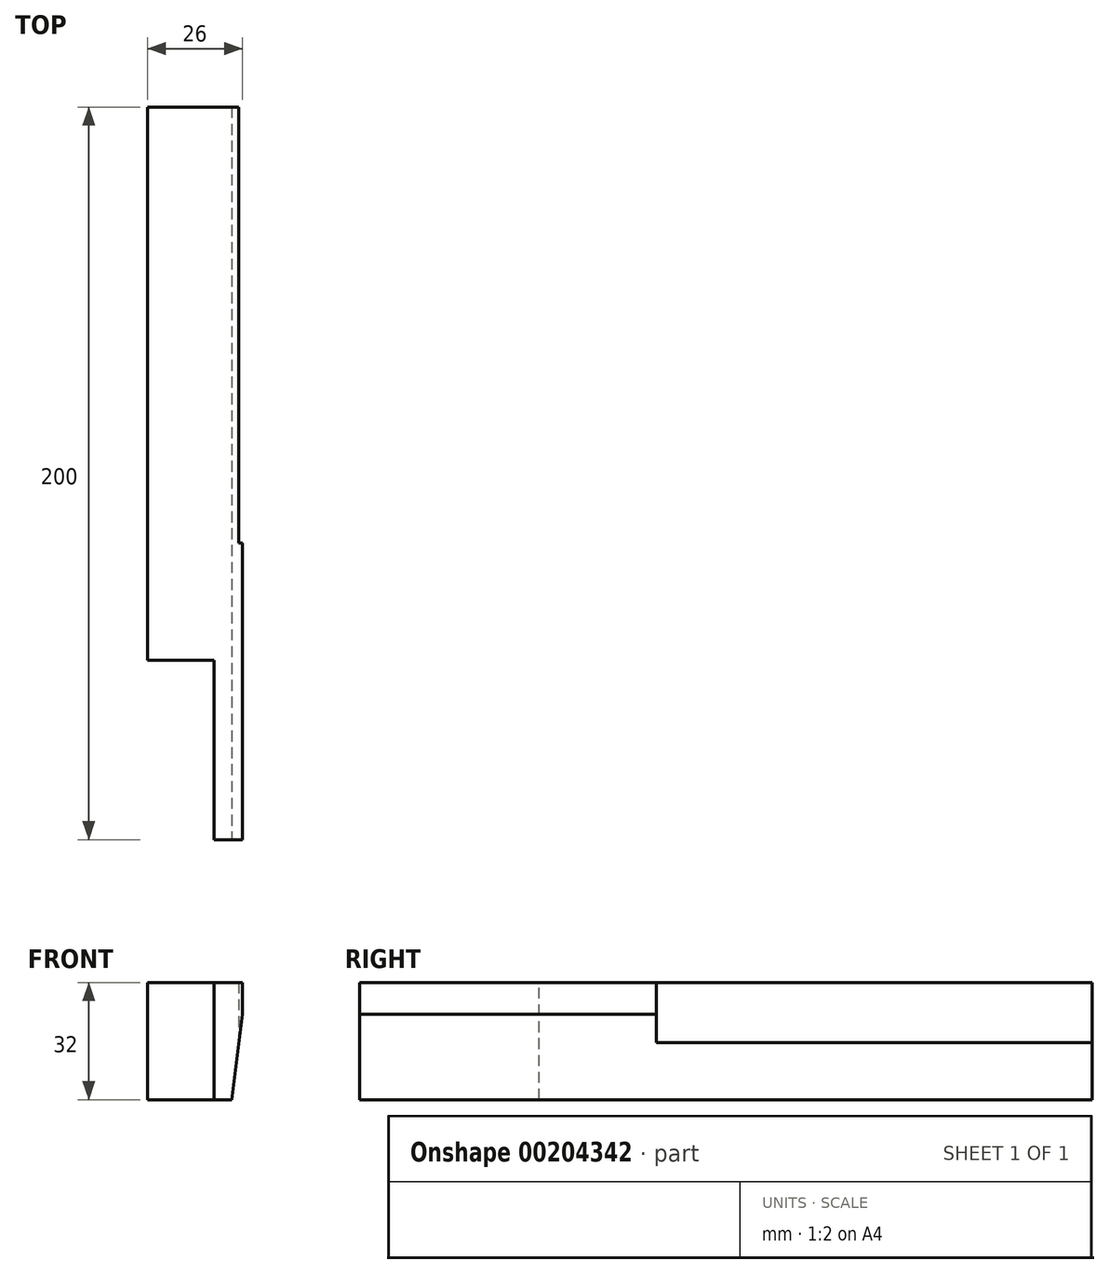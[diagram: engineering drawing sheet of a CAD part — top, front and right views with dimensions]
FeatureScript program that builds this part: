
annotation { "Feature Type Name" : "Feature", "Feature Type Description" : "" }
export const myFeature = defineFeature(function(context is Context, id is Id, definition is map)
    precondition{}
    {
        {
            var Q0;
            Q0=qCreatedBy(makeId("Front.planeOp"),FACE);
            var sketch = newSketch(context, id + "F0", { "sketchPlane" : qUnion([Q0])});
            skLineSegment(sketch, "E0.bottom", {"start": v(0, 0) * mm, "end": v(-25, 0) * mm});
            skLineSegment(sketch, "E0.top", {"start": v(0, -32) * mm, "end": v(-25, -32) * mm});
            skLineSegment(sketch, "E0.left", {"start": v(0, 0) * mm, "end": v(0, -32) * mm});
            skLineSegment(sketch, "E0.right", {"start": v(-25, 0) * mm, "end": v(-25, -32) * mm});
            skSolve(sketch);
        }
        {
            var Q0;
            Q0=makeQuery(id+"F0.imprint","IMPRINT",FACE,{"disambiguationData":[TD([[makeQuery(id+"F0.imprint","IMPRINT",EDGE,{"derivedFrom":sQuery(id+"F0.wireOp",EDGE,"E0.bottom")}),1.0]])]});
            extrude(context, id + "F1", {"entities" : qUnion([Q0]), "depth" : 151 * mm});
        }
        {
            var Q0;
            Q0=makeQuery(id+"F1.opExtrude","CAP_FACE",FACE,{"disambiguationData":[OSD([sQuery(id+"F0.wireOp",EDGE,"E0.bottom"),sQuery(id+"F0.wireOp",EDGE,"E0.top"),sQuery(id+"F0.wireOp",EDGE,"E0.left"),sQuery(id+"F0.wireOp",EDGE,"E0.right")])],"isStart":false});
            var sketch = newSketch(context, id + "F2", { "sketchPlane" : qUnion([Q0])});
            skLineSegment(sketch, "E1.bottom", {"start": v(0, -32) * mm, "end": v(-6.8, -32) * mm});
            skLineSegment(sketch, "E1.top", {"start": v(0, 0) * mm, "end": v(-6.8, 0) * mm});
            skLineSegment(sketch, "E1.left", {"start": v(0, -32) * mm, "end": v(0, 0) * mm});
            skLineSegment(sketch, "E1.right", {"start": v(-6.8, -32) * mm, "end": v(-6.8, 0) * mm});
            skSolve(sketch);
        }
        {
            var Q0;
            Q0 = qSketchRegion(id + "F2", true);
            extrude(context, id + "F3", {"entities" : qUnion([Q0]), "operationType" : NewBodyOperationType.ADD, "depth" : 49 * mm});
        }
        {
            var Q0;
            Q0=makeQuery(id+"F3.opExtrude","CAP_FACE",FACE,{"disambiguationData":[OSD([sQuery(id+"F2.wireOp",EDGE,"E1.bottom"),sQuery(id+"F2.wireOp",EDGE,"E1.top"),sQuery(id+"F2.wireOp",EDGE,"E1.left"),sQuery(id+"F2.wireOp",EDGE,"E1.right")])],"isStart":false});
            var sketch = newSketch(context, id + "F4", { "sketchPlane" : qUnion([Q0])});
            skLineSegment(sketch, "E2.bottom", {"start": v(0, -32) * mm, "end": v(1, -32) * mm});
            skLineSegment(sketch, "E2.top", {"start": v(0, 0) * mm, "end": v(1, 0) * mm});
            skLineSegment(sketch, "E2.left", {"start": v(0, -32) * mm, "end": v(0, 0) * mm});
            skLineSegment(sketch, "E2.right", {"start": v(1, -32) * mm, "end": v(1, 0) * mm});
            skSolve(sketch);
        }
        {
            var Q0;
            Q0=makeQuery(id+"F4.imprint","IMPRINT",FACE,{"disambiguationData":[TD([[makeQuery(id+"F4.imprint","IMPRINT",EDGE,{"derivedFrom":sQuery(id+"F4.wireOp",EDGE,"E2.bottom")}),1.0]])]});
            extrude(context, id + "F5", {"entities" : qUnion([Q0]), "operationType" : NewBodyOperationType.ADD, "oppositeDirection" : true, "depth" : 81 * mm});
        }
        {
            var Q0;
            Q0=makeQuery(id+"F1.opExtrude","CAP_FACE",FACE,{"disambiguationData":[OSD([sQuery(id+"F0.wireOp",EDGE,"E0.bottom"),sQuery(id+"F0.wireOp",EDGE,"E0.top"),sQuery(id+"F0.wireOp",EDGE,"E0.left"),sQuery(id+"F0.wireOp",EDGE,"E0.right")])],"isStart":true});
            var sketch = newSketch(context, id + "F6", { "sketchPlane" : qUnion([Q0])});
            skLineSegment(sketch, "E3", {"start": v(-1.42, -5.39) * mm, "end": v(2.83, -38.34) * mm});
            skLineSegment(sketch, "E4", {"start": v(2.83, -38.34) * mm, "end": v(-12.25, -38.34) * mm});
            skLineSegment(sketch, "E5", {"start": v(-12.25, -38.34) * mm, "end": v(-1.42, -5.39) * mm});
            skSolve(sketch);
        }
        {
            var Q0;
            Q0 = qSketchRegion(id + "F6", true);
            extrude(context, id + "F7", {"entities" : qUnion([Q0]), "operationType" : NewBodyOperationType.REMOVE, "oppositeDirection" : true, "depth" : 248 * mm});
        }
    });
